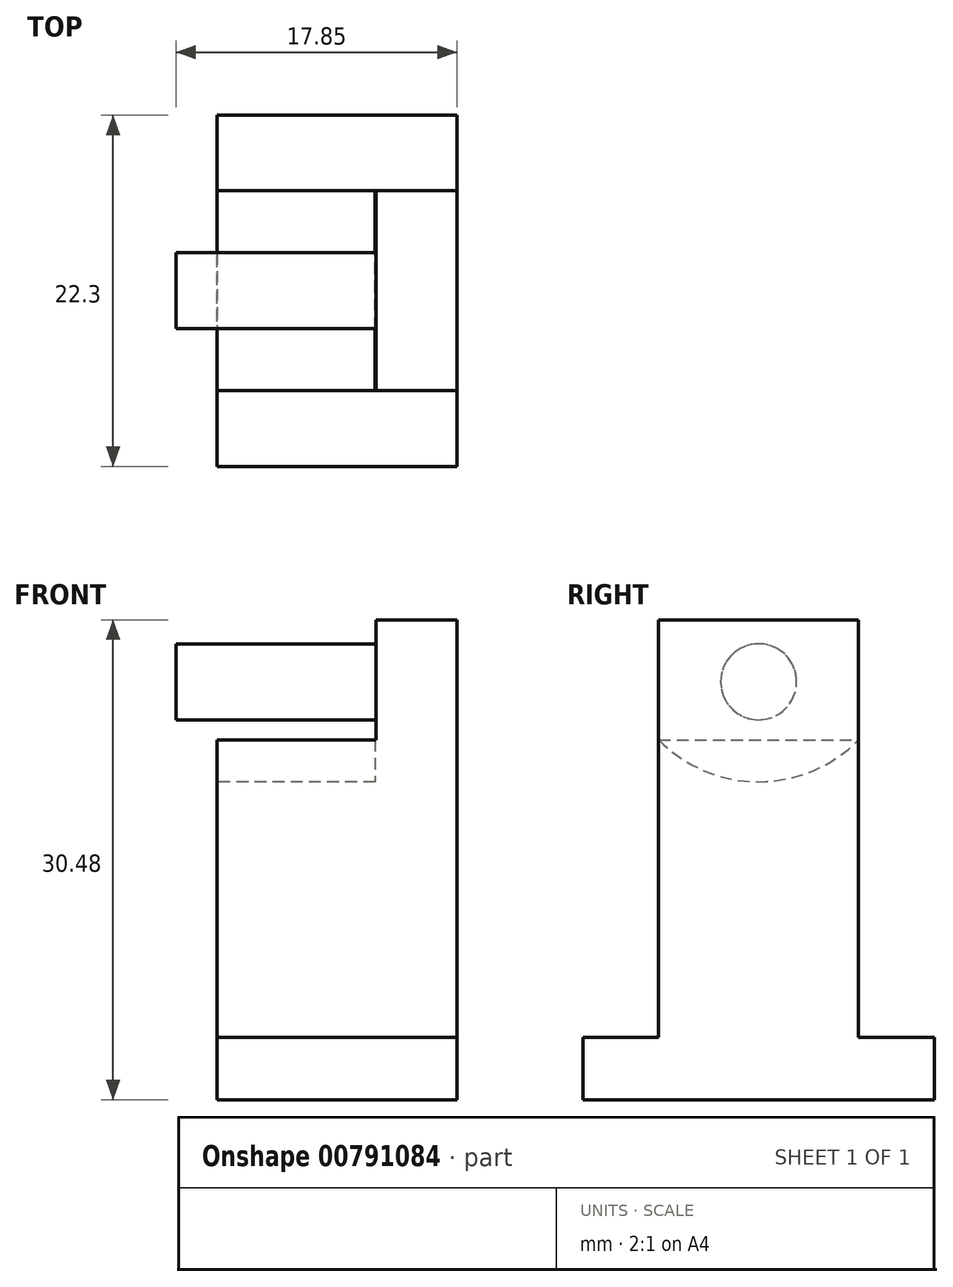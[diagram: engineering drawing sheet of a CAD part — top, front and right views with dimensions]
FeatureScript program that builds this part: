
annotation { "Feature Type Name" : "Feature", "Feature Type Description" : "" }
export const myFeature = defineFeature(function(context is Context, id is Id, definition is map)
    precondition{}
    {
        {
            var Q0;
            Q0=qCreatedBy(makeId("Front.planeOp"),FACE);
            var sketch = newSketch(context, id + "F0", { "sketchPlane" : qUnion([Q0])});
            skLineSegment(sketch, "E0", {"start": v(10.1, 0) * mm, "end": v(15.24, 0) * mm});
            skLineSegment(sketch, "E1", {"start": v(15.24, 0) * mm, "end": v(15.24, -30.48) * mm});
            skLineSegment(sketch, "E2", {"start": v(15.24, -30.48) * mm, "end": v(0, -30.48) * mm});
            skLineSegment(sketch, "E3", {"start": v(0, -30.48) * mm, "end": v(0, -7.62) * mm});
            skLineSegment(sketch, "E4", {"start": v(10.1, 0) * mm, "end": v(10.1, -7.62) * mm});
            skLineSegment(sketch, "E5", {"start": v(10.1, -7.62) * mm, "end": v(0, -7.62) * mm});
            skSolve(sketch);
        }
        {
            var Q0;
            Q0=makeQuery(id+"F0.imprint","IMPRINT",FACE,{"disambiguationData":[TD([[makeQuery(id+"F0.imprint","IMPRINT",EDGE,{"derivedFrom":sQuery(id+"F0.wireOp",EDGE,"E0")}),-1.0]])]});
            extrude(context, id + "F1", {"entities" : qUnion([Q0]), "depth" : 12.7 * mm, "offsetDistance" : 25.4 * mm});
        }
        {
            var Q0;
            Q0=makeQuery(id+"F1.opExtrude","CAP_FACE",FACE,{"disambiguationData":[OSD([sQuery(id+"F0.wireOp",EDGE,"E0"),sQuery(id+"F0.wireOp",EDGE,"E1"),sQuery(id+"F0.wireOp",EDGE,"E2"),sQuery(id+"F0.wireOp",EDGE,"E3"),sQuery(id+"F0.wireOp",EDGE,"E4"),sQuery(id+"F0.wireOp",EDGE,"E5")])],"isStart":false});
            var sketch = newSketch(context, id + "F2", { "sketchPlane" : qUnion([Q0])});
            skLineSegment(sketch, "E6.bottom", {"start": v(0, -26.52) * mm, "end": v(15.24, -26.52) * mm});
            skLineSegment(sketch, "E6.top", {"start": v(0, -30.48) * mm, "end": v(15.24, -30.48) * mm});
            skLineSegment(sketch, "E6.left", {"start": v(0, -26.52) * mm, "end": v(0, -30.48) * mm});
            skLineSegment(sketch, "E6.right", {"start": v(15.24, -26.52) * mm, "end": v(15.24, -30.48) * mm});
            skSolve(sketch);
        }
        {
            var Q0;
            Q0 = qSketchRegion(id + "F2", true);
            extrude(context, id + "F3", {"entities" : qUnion([Q0]), "operationType" : NewBodyOperationType.ADD, "depth" : 4.8 * mm, "offsetDistance" : 25.4 * mm});
        }
        {
            var Q0;
            Q0=makeQuery(id+"F3.boolean.opBoolean","MERGE",FACE,{"derivedFrom":[makeQuery(id+"F1.opExtrude","SWEPT_FACE",FACE,{"disambiguationData":[OSD([sQuery(id+"F0.wireOp",EDGE,"E3")])]}),makeQuery(id+"F3.opExtrude","SWEPT_FACE",FACE,{"disambiguationData":[OSD([sQuery(id+"F2.wireOp",EDGE,"E6.left")])]})]});
            var sketch = newSketch(context, id + "F4", { "sketchPlane" : qUnion([Q0])});
            skArc(sketch, "E7", {"start": v(0, -7.62) * mm, "mid": v(6.35, -10.29) * mm, "end": v(12.7, -7.62) * mm});
            skLineSegment(sketch, "E8", {"start": v(0, -7.62) * mm, "end": v(12.7, -7.62) * mm});
            skSolve(sketch);
        }
        {
            var Q0;
            Q0=makeQuery(id+"F4.imprint","IMPRINT",FACE,{"disambiguationData":[TD([[makeQuery(id+"F4.imprint","IMPRINT",EDGE,{"derivedFrom":sQuery(id+"F4.wireOp",EDGE,"E7")}),1.0]])]});
            extrude(context, id + "F5", {"entities" : qUnion([Q0]), "operationType" : NewBodyOperationType.REMOVE, "oppositeDirection" : true, "depth" : 10.03 * mm, "offsetDistance" : 25.4 * mm});
        }
        {
            var Q0;
            Q0=makeQuery(id+"F1.opExtrude","SWEPT_FACE",FACE,{"disambiguationData":[OSD([sQuery(id+"F0.wireOp",EDGE,"E4")])]});
            var sketch = newSketch(context, id + "F6", { "sketchPlane" : qUnion([Q0])});
            skCircle(sketch, "E9", {"center": v(6.35, -3.94) * mm, "radius": 2.41 * mm});
            skPoint(sketch, "E9.centerSnap0", {"position": v(6.35, 0) * mm});
            skSolve(sketch);
        }
        {
            var Q0;
            Q0 = qSketchRegion(id + "F6", true);
            extrude(context, id + "F7", {"entities" : qUnion([Q0]), "operationType" : NewBodyOperationType.ADD, "depth" : 12.7 * mm, "offsetDistance" : 25.4 * mm});
        }
        {
            var Q0;
            Q0=makeQuery(id+"F1.opExtrude","CAP_FACE",FACE,{"disambiguationData":[OSD([sQuery(id+"F0.wireOp",EDGE,"E0"),sQuery(id+"F0.wireOp",EDGE,"E1"),sQuery(id+"F0.wireOp",EDGE,"E2"),sQuery(id+"F0.wireOp",EDGE,"E3"),sQuery(id+"F0.wireOp",EDGE,"E4"),sQuery(id+"F0.wireOp",EDGE,"E5")])],"isStart":true});
            var sketch = newSketch(context, id + "F8", { "sketchPlane" : qUnion([Q0])});
            skLineSegment(sketch, "E10.bottom", {"start": v(-15.24, -30.48) * mm, "end": v(0, -30.48) * mm});
            skLineSegment(sketch, "E10.top", {"start": v(-15.24, -26.52) * mm, "end": v(0, -26.52) * mm});
            skLineSegment(sketch, "E10.left", {"start": v(-15.24, -30.48) * mm, "end": v(-15.24, -26.52) * mm});
            skLineSegment(sketch, "E10.right", {"start": v(0, -30.48) * mm, "end": v(0, -26.52) * mm});
            skSolve(sketch);
        }
        {
            var Q0;
            Q0=makeQuery(id+"F8.imprint","IMPRINT",FACE,{"disambiguationData":[TD([[makeQuery(id+"F8.imprint","IMPRINT",EDGE,{"derivedFrom":sQuery(id+"F8.wireOp",EDGE,"E10.bottom")}),1.0]])]});
            extrude(context, id + "F9", {"entities" : qUnion([Q0]), "operationType" : NewBodyOperationType.ADD, "depth" : 4.8 * mm, "offsetDistance" : 25.4 * mm});
        }
    });
